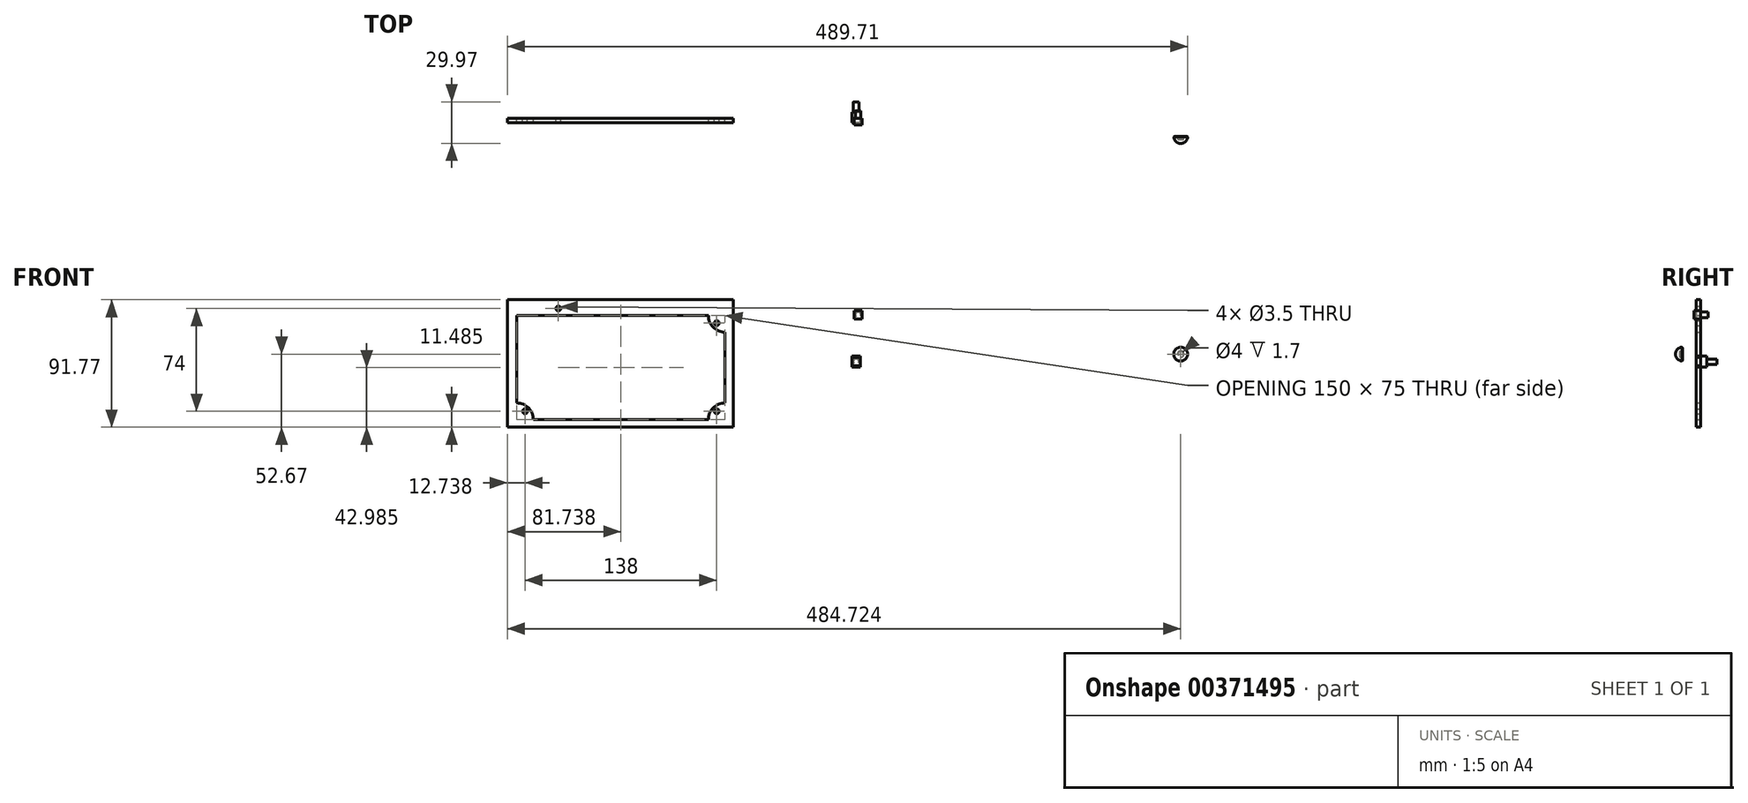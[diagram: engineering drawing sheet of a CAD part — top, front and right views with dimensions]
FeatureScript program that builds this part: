
annotation { "Feature Type Name" : "Feature", "Feature Type Description" : "" }
export const myFeature = defineFeature(function(context is Context, id is Id, definition is map)
    precondition{}
    {
        {
            var Q0;
            Q0=qCreatedBy(makeId("Front.planeOp"),FACE);
            var sketch = newSketch(context, id + "F0", { "sketchPlane" : qUnion([Q0])});
            skLineSegment(sketch, "E0", {"start": v(-111.14, 52.81) * mm, "end": v(26.86, 52.81) * mm});
            skLineSegment(sketch, "E1", {"start": v(38.86, 40.81) * mm, "end": v(38.86, -10.19) * mm});
            skLineSegment(sketch, "E2", {"start": v(-111.14, 52.81) * mm, "end": v(-111.14, -10.19) * mm});
            skLineSegment(sketch, "E3", {"start": v(-99.14, -22.19) * mm, "end": v(26.86, -22.19) * mm});
            skArc(sketch, "E4", {"start": v(26.86, 52.81) * mm, "mid": v(30.37, 44.33) * mm, "end": v(38.86, 40.81) * mm});
            skArc(sketch, "E5", {"start": v(38.86, -10.19) * mm, "mid": v(30.37, -13.7) * mm, "end": v(26.86, -22.19) * mm});
            skArc(sketch, "E6", {"start": v(-99.14, -22.19) * mm, "mid": v(-102.66, -13.7) * mm, "end": v(-111.14, -10.19) * mm});
            skCircle(sketch, "E7", {"center": v(-105.14, -16.19) * mm, "radius": 1.75 * mm});
            skCircle(sketch, "E8", {"center": v(32.86, 47.31) * mm, "radius": 1.75 * mm});
            skCircle(sketch, "E9", {"center": v(32.86, -16.19) * mm, "radius": 1.75 * mm});
            skCircle(sketch, "E10", {"center": v(-81.14, 57.81) * mm, "radius": 1.75 * mm});
            skLineSegment(sketch, "E11.bottom", {"start": v(-117.88, 64.1) * mm, "end": v(44.82, 64.1) * mm});
            skLineSegment(sketch, "E11.top", {"start": v(-117.88, -27.67) * mm, "end": v(44.82, -27.67) * mm});
            skLineSegment(sketch, "E11.left", {"start": v(-117.88, 64.1) * mm, "end": v(-117.88, -27.67) * mm});
            skLineSegment(sketch, "E11.right", {"start": v(44.82, 64.1) * mm, "end": v(44.82, -27.67) * mm});
            skSolve(sketch);
        }
        {
            var Q0;
            Q0=makeQuery(id+"F0.imprint","IMPRINT",FACE,{"disambiguationData":[TD([[makeQuery(id+"F0.imprint","IMPRINT",EDGE,{"derivedFrom":sQuery(id+"F0.wireOp",EDGE,"E0")}),1.0]])]});
            extrude(context, id + "F1", {"entities" : qUnion([Q0]), "depth" : 3 * mm});
        }
        {
            var Q0;
            Q0=qCreatedBy(makeId("Front.planeOp"),FACE);
            var sketch = newSketch(context, id + "F2", { "sketchPlane" : qUnion([Q0])});
            skLineSegment(sketch, "E12.bottom", {"start": v(137.63, 56.25) * mm, "end": v(131.63, 56.25) * mm});
            skLineSegment(sketch, "E12.top", {"start": v(137.63, 50.25) * mm, "end": v(131.63, 50.25) * mm});
            skLineSegment(sketch, "E12.left", {"start": v(137.63, 56.25) * mm, "end": v(137.63, 50.25) * mm});
            skLineSegment(sketch, "E12.right", {"start": v(131.63, 56.25) * mm, "end": v(131.63, 50.25) * mm});
            skSolve(sketch);
        }
        {
            var Q0;
            Q0=makeQuery(id+"F2.imprint","IMPRINT",FACE,{"disambiguationData":[TD([[makeQuery(id+"F2.imprint","IMPRINT",EDGE,{"derivedFrom":sQuery(id+"F2.wireOp",EDGE,"E12.bottom")}),1.0]])]});
            extrude(context, id + "F3", {"entities" : qUnion([Q0]), "depth" : 4.5 * mm});
        }
        {
            var Q0;
            Q0=makeQuery(id+"F3.opExtrude","CAP_FACE",FACE,{"disambiguationData":[OSD([sQuery(id+"F2.wireOp",EDGE,"E12.bottom"),sQuery(id+"F2.wireOp",EDGE,"E12.top"),sQuery(id+"F2.wireOp",EDGE,"E12.left"),sQuery(id+"F2.wireOp",EDGE,"E12.right")])],"isStart":true});
            var sketch = newSketch(context, id + "F4", { "sketchPlane" : qUnion([Q0])});
            skCircle(sketch, "E13", {"center": v(-134.63, 53.25) * mm, "radius": 1.95 * mm});
            skPoint(sketch, "E13.centerSnap0", {"position": v(-131.63, 53.25) * mm});
            skPoint(sketch, "E13.centerSnap1", {"position": v(-134.63, 56.25) * mm});
            skSolve(sketch);
        }
        {
            var Q0;
            Q0=makeQuery(id+"F4.imprint","IMPRINT",FACE,{"disambiguationData":[TD([[makeQuery(id+"F4.imprint","IMPRINT",EDGE,{"derivedFrom":sQuery(id+"F4.wireOp",EDGE,"E13")}),1.0]])]});
            extrude(context, id + "F5", {"entities" : qUnion([Q0]), "operationType" : NewBodyOperationType.ADD, "depth" : 5.5 * mm, "offsetDistance" : 25 * mm});
        }
        {
            var Q0;
            Q0=qCreatedBy(makeId("Front.planeOp"),FACE);
            var sketch = newSketch(context, id + "F6", { "sketchPlane" : qUnion([Q0])});
            skLineSegment(sketch, "E14.bottom", {"start": v(136.2, 22.55) * mm, "end": v(130.2, 22.55) * mm});
            skLineSegment(sketch, "E14.top", {"start": v(136.2, 16.45) * mm, "end": v(130.2, 16.45) * mm});
            skLineSegment(sketch, "E15.bottom", {"start": v(136.2, 23.55) * mm, "end": v(130.2, 23.55) * mm});
            skLineSegment(sketch, "E15.top", {"start": v(136.2, 15.55) * mm, "end": v(130.2, 15.55) * mm});
            skLineSegment(sketch, "E15.left", {"start": v(136.2, 23.55) * mm, "end": v(136.2, 22.55) * mm});
            skLineSegment(sketch, "E15.right", {"start": v(130.2, 23.55) * mm, "end": v(130.2, 22.55) * mm});
            skLineSegment(sketch, "E16.trimOffspring", {"start": v(136.2, 16.45) * mm, "end": v(136.2, 15.55) * mm});
            skLineSegment(sketch, "E17.trimOffspring", {"start": v(130.2, 16.45) * mm, "end": v(130.2, 15.55) * mm});
            skSolve(sketch);
        }
        {
            var Q0;
            Q0 = qSketchRegion(id + "F6", true);
            extrude(context, id + "F7", {"entities" : qUnion([Q0]), "depth" : 3 * mm});
        }
        {
            var Q0;
            Q0=makeQuery(id+"F7.opExtrude","CAP_FACE",FACE,{"disambiguationData":[OSD([sQuery(id+"F6.wireOp",EDGE,"E14.bottom"),sQuery(id+"F6.wireOp",EDGE,"E15.bottom"),sQuery(id+"F6.wireOp",EDGE,"E15.left"),sQuery(id+"F6.wireOp",EDGE,"E15.right")])],"isStart":true});
            var sketch = newSketch(context, id + "F8", { "sketchPlane" : qUnion([Q0])});
            skLineSegment(sketch, "E18.bottom", {"start": v(-136.2, 23.55) * mm, "end": v(-130.2, 23.55) * mm});
            skLineSegment(sketch, "E18.top", {"start": v(-136.2, 15.55) * mm, "end": v(-130.2, 15.55) * mm});
            skLineSegment(sketch, "E18.left", {"start": v(-136.2, 23.55) * mm, "end": v(-136.2, 15.55) * mm});
            skLineSegment(sketch, "E18.right", {"start": v(-130.2, 23.55) * mm, "end": v(-130.2, 15.55) * mm});
            skSolve(sketch);
        }
        {
            var Q0;
            Q0 = qSketchRegion(id + "F8", true);
            extrude(context, id + "F9", {"entities" : qUnion([Q0]), "depth" : 4.5 * mm});
        }
        {
            var Q0;
            Q0=makeQuery(id+"F9.opExtrude","CAP_FACE",FACE,{"disambiguationData":[OSD([sQuery(id+"F8.wireOp",EDGE,"E18.bottom"),sQuery(id+"F8.wireOp",EDGE,"E18.top"),sQuery(id+"F8.wireOp",EDGE,"E18.left"),sQuery(id+"F8.wireOp",EDGE,"E18.right")])],"isStart":false});
            var sketch = newSketch(context, id + "F10", { "sketchPlane" : qUnion([Q0])});
            skCircle(sketch, "E19", {"center": v(-133.2, 19.55) * mm, "radius": 1.95 * mm});
            skPoint(sketch, "E19.centerSnap0", {"position": v(-130.2, 19.55) * mm});
            skPoint(sketch, "E19.centerSnap1", {"position": v(-133.2, 23.55) * mm});
            skSolve(sketch);
        }
        {
            var Q0;
            Q0=makeQuery(id+"F10.imprint","IMPRINT",FACE,{"disambiguationData":[TD([[makeQuery(id+"F10.imprint","IMPRINT",EDGE,{"derivedFrom":sQuery(id+"F10.wireOp",EDGE,"E19")}),1.0]])]});
            extrude(context, id + "F11", {"entities" : qUnion([Q0]), "operationType" : NewBodyOperationType.ADD, "depth" : 7.5 * mm});
        }
        {
            var Q0;
            Q0=sQuery(id+"FwnAhbYVnTsRaz3_5.wireOp",VERTEX,"6148daeb-1146-40ba-acfd-df080c2a062e");
            var Q1;
            Q1=sQuery(id+"FwnAhbYVnTsRaz3_5.wireOp",VERTEX,"f8e88b70-3989-4e2c-90d6-8c6dce72787b");
            var Q2;
            Q2=qCreatedBy(makeId("Top.planeOp"),FACE);
            cPlane(context, id + "F12", {"entities" : qUnion([Q0, Q1, Q2]), "cplaneType" : CPlaneType.OFFSET, "offset" : 25 * mm, "width" : 150 * mm, "height" : 150 * mm});
        }
        {
            var Q0;
            Q0=qCreatedBy(id+"F12.planeOp",FACE);
            var sketch = newSketch(context, id + "F13", { "sketchPlane" : qUnion([Q0])});
            skLineSegment(sketch, "E20", {"start": v(366.84, 0) * mm, "end": v(366.84, -12.97) * mm});
            skPoint(sketch, "E21", {"position": v(366.84, -12.97) * mm});
            skArc(sketch, "E22", {"start": v(366.84, -17.97) * mm, "mid": v(370.38, -16.5) * mm, "end": v(371.84, -12.97) * mm});
            skPoint(sketch, "E23", {"position": v(366.84, -14.97) * mm});
            skPoint(sketch, "E24", {"position": v(368.84, -12.97) * mm});
            skLineSegment(sketch, "E25", {"start": v(366.84, -14.97) * mm, "end": v(368.84, -14.97) * mm});
            skLineSegment(sketch, "E26", {"start": v(368.84, -14.97) * mm, "end": v(368.84, -12.97) * mm});
            skLineSegment(sketch, "E27.trimOffspring", {"start": v(366.84, -14.97) * mm, "end": v(366.84, -26.46) * mm});
            skLineSegment(sketch, "E28.trimOffspring", {"start": v(368.84, -12.97) * mm, "end": v(371.84, -12.97) * mm});
            skSolve(sketch);
        }
        {
            var Q0;
            {var subQ1=sQuery(id+"F13.wireOp",EDGE,"E22");Q0=makeQuery(id+"F13.imprint","IMPRINT",FACE,{"disambiguationData":[TD([[makeQuery(id+"F13.imprint","IMPRINT",EDGE,{"derivedFrom":subQ1}),1.0]])]});}
            var Q1;
            Q1=sQuery(id+"F13.wireOp",EDGE,"E27.trimOffspring");
            revolve(context, id + "F14", {"entities" : qUnion([Q0]), "axis" : qUnion([Q1]), "revolveType" : RevolveType.FULL});
        }
        {
            var Q0;
            Q0=makeQuery(id+"F14.opRevolve","SWEPT_EDGE",EDGE,{"disambiguationData":[OSD([sQuery(id+"F13.wireOp",EDGE,"E26"),sQuery(id+"F13.wireOp",EDGE,"E28.trimOffspring")])]});
            var Q1;
            Q1=makeQuery(id+"F14.opRevolve","SWEPT_EDGE",EDGE,{"disambiguationData":[OSD([sQuery(id+"F13.wireOp",EDGE,"E22"),sQuery(id+"F13.wireOp",EDGE,"E28.trimOffspring")])]});
            chamfer(context, id + "F15", {"entities" : qUnion([Q0, Q1]), "width" : 0.3 * mm, "tangentPropagation" : true});
        }
    });
